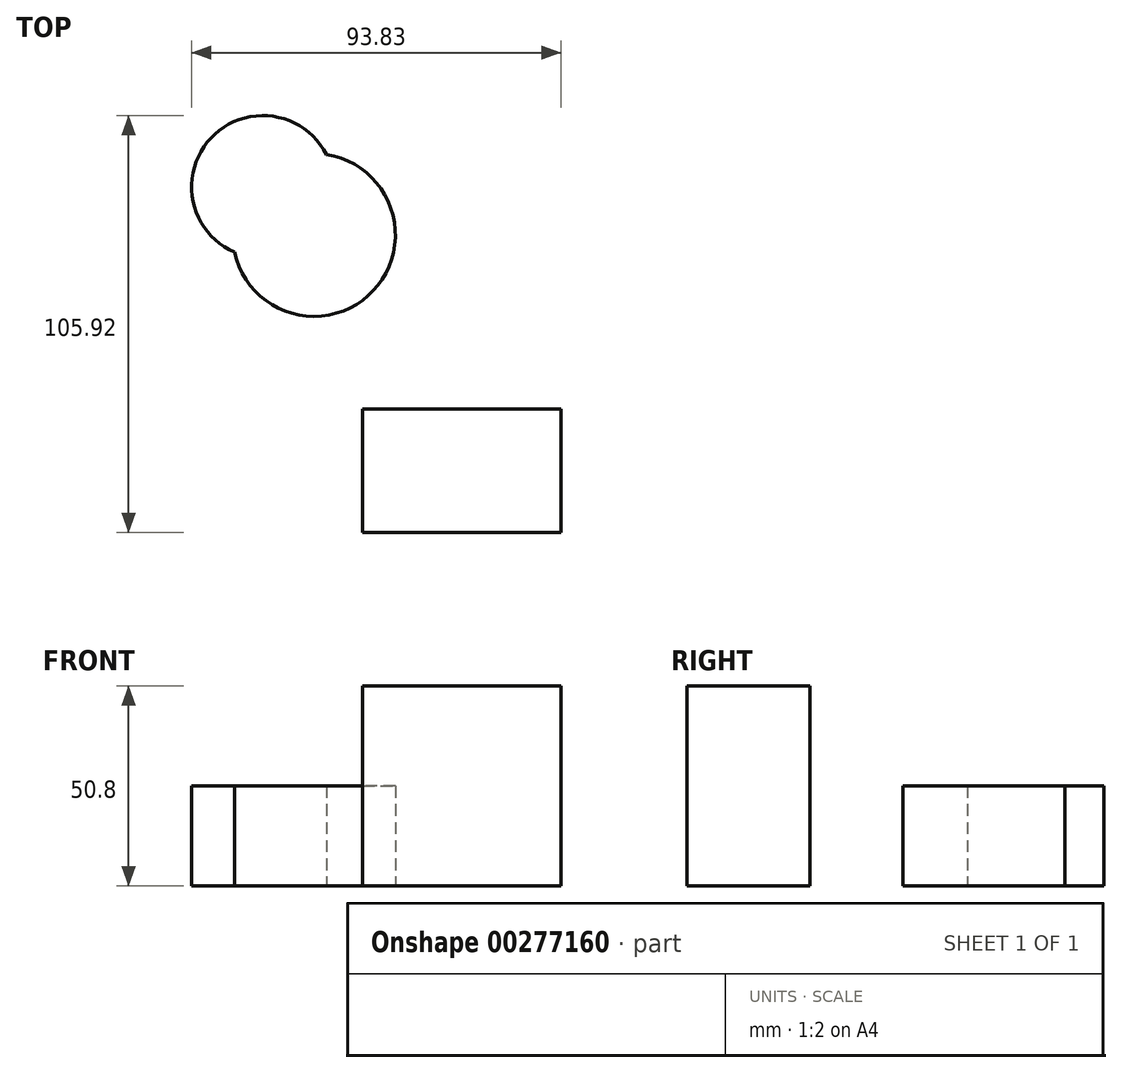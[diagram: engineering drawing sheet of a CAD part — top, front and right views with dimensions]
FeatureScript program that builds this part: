
annotation { "Feature Type Name" : "Feature", "Feature Type Description" : "" }
export const myFeature = defineFeature(function(context is Context, id is Id, definition is map)
    precondition{}
    {
        {
            var Q0;
            Q0=qCreatedBy(makeId("Top.planeOp"),FACE);
            var sketch = newSketch(context, id + "F0", { "sketchPlane" : qUnion([Q0])});
            skCircle(sketch, "E0", {"center": v(-47.55, 53.47) * mm, "radius": 18.1 * mm});
            skCircle(sketch, "E1", {"center": v(-34.56, 41.25) * mm, "radius": 20.67 * mm});
            skSolve(sketch);
        }
        {
            var Q0;
            {var subQ0=sQuery(id+"F0.wireOp",EDGE,"E1");var subQ1=sQuery(id+"F0.wireOp",EDGE,"E0");var subQ2=makeQuery(id+"F0.imprint","INTERSECT",VERTEX,{"disambiguationData":[OD(0.0)],"derivedFrom":[subQ1,subQ0]});Q0=makeQuery(id+"F0.imprint","IMPRINT",FACE,{"disambiguationData":[TD([[makeQuery(id+"F0.imprint","IMPRINT",EDGE,{"disambiguationData":[TD([[subQ2,-1.0]])],"derivedFrom":subQ1}),1.0]])]});}
            var Q1;
            {var subQ0=sQuery(id+"F0.wireOp",EDGE,"E1");var subQ1=sQuery(id+"F0.wireOp",EDGE,"E0");var subQ2=makeQuery(id+"F0.imprint","INTERSECT",VERTEX,{"disambiguationData":[OD(0.0)],"derivedFrom":[subQ1,subQ0]});Q1=makeQuery(id+"F0.imprint","IMPRINT",FACE,{"disambiguationData":[TD([[makeQuery(id+"F0.imprint","IMPRINT",EDGE,{"disambiguationData":[TD([[subQ2,-1.0]])],"derivedFrom":subQ1}),-1.0]])]});}
            var Q2;
            {var subQ0=sQuery(id+"F0.wireOp",EDGE,"E1");var subQ1=sQuery(id+"F0.wireOp",EDGE,"E0");var subQ2=makeQuery(id+"F0.imprint","INTERSECT",VERTEX,{"disambiguationData":[OD(0.0)],"derivedFrom":[subQ1,subQ0]});Q2=makeQuery(id+"F0.imprint","IMPRINT",FACE,{"disambiguationData":[TD([[makeQuery(id+"F0.imprint","IMPRINT",EDGE,{"disambiguationData":[TD([[subQ2,1.0]])],"derivedFrom":subQ1}),1.0]])]});}
            extrude(context, id + "F1", {"entities" : qUnion([Q0, Q1, Q2]), "depth" : 25.4 * mm});
        }
        {
            var Q0;
            Q0=qCreatedBy(makeId("Top.planeOp"),FACE);
            var sketch = newSketch(context, id + "F2", { "sketchPlane" : qUnion([Q0])});
            skLineSegment(sketch, "E2.bottom", {"start": v(-22.24, -3.03) * mm, "end": v(28.18, -3.03) * mm});
            skLineSegment(sketch, "E2.top", {"start": v(-22.24, -34.35) * mm, "end": v(28.18, -34.35) * mm});
            skLineSegment(sketch, "E2.left", {"start": v(-22.24, -3.03) * mm, "end": v(-22.24, -34.35) * mm});
            skLineSegment(sketch, "E2.right", {"start": v(28.18, -3.03) * mm, "end": v(28.18, -34.35) * mm});
            skSolve(sketch);
        }
        {
            var Q0;
            Q0 = qSketchRegion(id + "F2", true);
            extrude(context, id + "F3", {"entities" : qUnion([Q0]), "depth" : 50.8 * mm});
        }
    });
